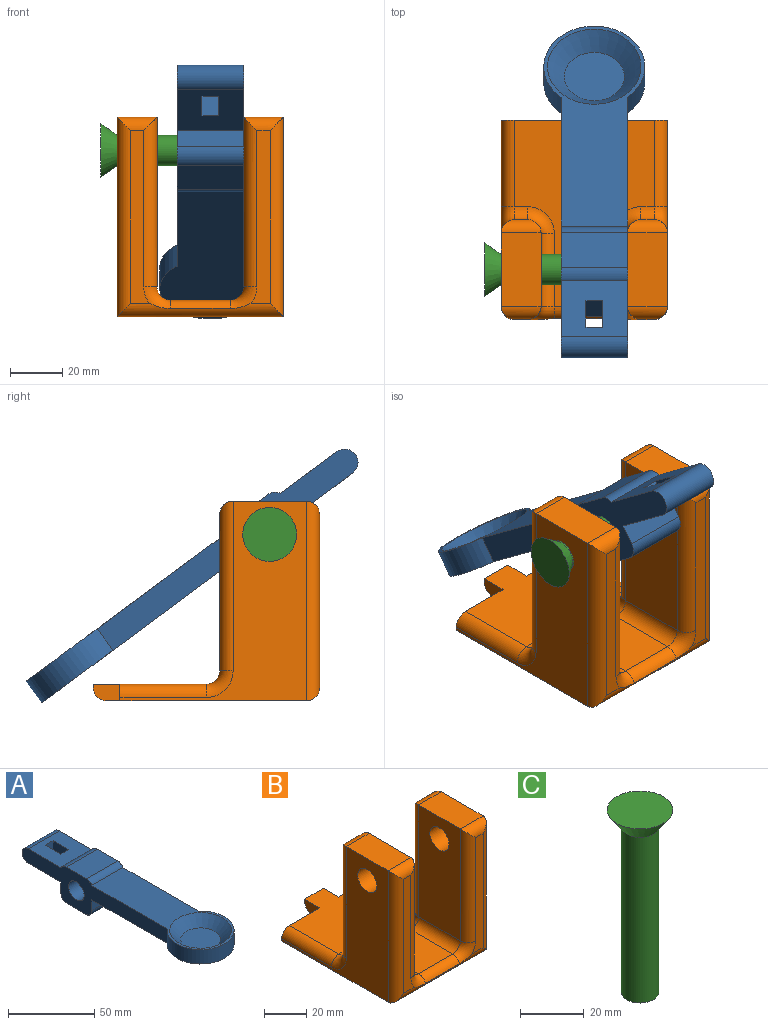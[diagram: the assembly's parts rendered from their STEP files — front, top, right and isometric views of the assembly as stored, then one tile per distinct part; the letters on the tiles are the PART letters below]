
ASSEMBLY  parts=3 mates=3
PART A: 23 faces, bbox 38.6x152.7x25.4 mm
  f0: plane 26.67x25.4mm, normal (0,0,1), area 596.8mm2, adj f2,f3,f4,f5,f7,f8,f20,f22
  f1: plane 26.67x25.4mm, normal (0,0,-1), area 596.8mm2, adj f2,f3,f4,f5,f7,f8,f12,f22
  f2: plane 12.7x10.16mm, normal (-1,0,0), area 129mm2, adj f0,f1,f3,f8
  f3: plane 10.16x6.35mm, normal (0,1,0), area 64.5mm2, adj f0,f1,f2,f4
  f4: plane 12.7x10.16mm, normal (1,0,0), area 129mm2, adj f0,f1,f3,f8
  f5: plane 118.81x25.4mm, normal (-1,0,0), area 1438.9mm2, adj f0,f1,f6,f9,f10,f11,f12,f13
  f6: cylinder r=19.3mm len=38.61mm, axis (0,0,-1), area 950.7mm2, adj f5,f7,f9,f10
  f7: plane 118.81x25.4mm, normal (1,0,0), area 1438.9mm2, adj f0,f1,f6,f9,f10,f11,f12,f13
  f8: plane 10.16x6.35mm, normal (0,-1,0), area 64.5mm2, adj f0,f1,f2,f4
  f9: plane 95.51x38.61mm, normal (0,0,1), area 1654.1mm2, adj f5,f6,f7,f17,f21
  f10: plane 95.51x38.61mm, normal (0,0,-1), area 2654.1mm2, adj f5,f6,f7,f13
  f11: plane 25.4x15.24mm, normal (0,0,-1), area 387.1mm2, adj f5,f7,f18,f19
  f12: plane 25.4x7.62mm, normal (0,1,0), area 193.5mm2, adj f1,f5,f7,f18
  f13: plane 25.4x7.62mm, normal (0,-1,0), area 193.5mm2, adj f5,f7,f10,f19
  f14: plane 25.4x16.6mm, normal (0,0,1), area 421.7mm2, adj f5,f7,f20,f21
  f15: cylinder r=6.35mm len=25.4mm, axis (1,0,0), area 1013.4mm2, adj f5,f7
  f16: plane 22.98x22.98mm, normal (0,0,1), area 414.8mm2, adj f17
  f17: cone r=8.95mm half-angle=45deg, axis (0,0,1), area 827.5mm2, adj f9,f16
  f18: cylinder r=5.08mm len=25.4mm, axis (-1,0,0), area 202.7mm2, adj f5,f7,f11,f12
  f19: cylinder r=5.08mm len=25.4mm, axis (1,0,0), area 202.7mm2, adj f5,f7,f11,f13
  f20: cylinder r=5.08mm len=25.4mm, axis (-1,0,0), area 135.1mm2, adj f0,f5,f7,f14
  f21: cylinder r=5.08mm len=25.4mm, axis (-1,0,0), area 135.1mm2, adj f5,f7,f9,f14
  f22: cylinder r=5.08mm len=25.4mm, axis (1,0,0), area 405.4mm2, adj f0,f1,f5,f7
PART B: 46 faces, bbox 63.5x86.4x79.7 mm
  f0: plane 66.04x7.31mm, normal (0,-1,0), area 340mm2, adj f31,f32,f37,f38,f42
  f1: plane 25.4x6.35mm, normal (0,1,0), area 155.8mm2, adj f2,f6,f7,f18,f20
  f2: plane 81.28x53.34mm, normal (0,0,1), area 2805.6mm2, adj f1,f5,f16,f17,f18,f20,f24,f25
  f3: plane 66.04x7.31mm, normal (0,-1,0), area 340mm2, adj f26,f27,f33,f34,f38
  f4: plane 76.2x71.12mm, normal (1,0,0), area 2079.3mm2, adj f5,f7,f13,f14,f29,f30,f32,f35
  f5: plane 25.4x6.35mm, normal (0,1,0), area 155.8mm2, adj f2,f4,f7,f16,f29
  f6: plane 76.2x71.12mm, normal (-1,0,0), area 2079.3mm2, adj f1,f7,f10,f15,f19,f20,f22,f33
  f7: plane 76.2x63.5mm, normal (0,0,-1), area 4580.6mm2, adj f1,f4,f5,f6,f16,f18,f38,f45
  f8: plane 59.69x5.08mm, normal (0,1,0), area 303.2mm2, adj f19,f21,f23,f24
  f9: plane 64.77x27.94mm, normal (1,0,0), area 1683mm2, adj f10,f15,f23,f27,f28
  f10: plane 27.94x15.24mm, normal (0,0,1), area 425.8mm2, adj f6,f9,f21,f26
  f11: plane 59.69x5.08mm, normal (0,1,0), area 303.2mm2, adj f30,f36,f40,f41
  f12: plane 64.77x27.94mm, normal (-1,0,0), area 1683mm2, adj f13,f14,f37,f41,f44
  f13: plane 27.94x15.24mm, normal (0,0,1), area 425.8mm2, adj f4,f12,f31,f36
  f14: cylinder r=6.35mm len=15.24mm, axis (1,0,0), area 608mm2, adj f4,f12
  f15: cylinder r=6.35mm len=15.24mm, axis (1,0,0), area 608mm2, adj f6,f9
  f16: plane 10.16x6.35mm, normal (1,0,0), area 59mm2, adj f2,f5,f7,f17,f45
  f17: plane 12.7x1.27mm, normal (0,1,0), area 16.1mm2, adj f2,f16,f18,f45
  f18: plane 10.16x6.35mm, normal (-1,0,0), area 59mm2, adj f1,f2,f7,f17,f45
  f19: cylinder r=5.08mm len=64.77mm, axis (0,0,-1), area 502.1mm2, adj f6,f8,f21,f22
  f20: cylinder r=5.08mm len=33.02mm, axis (0,1,0), area 263.5mm2, adj f1,f2,f6,f22
  f21: cylinder r=5.08mm len=15.24mm, axis (1,0,0), area 92.1mm2, adj f8,f10,f19,f23
  f22: torus R=10.16mm, axis (-1,0,0), area 86.8mm2, adj f6,f19,f20,f24
  f23: cylinder r=5.08mm len=64.77mm, axis (0,0,-1), area 502.1mm2, adj f8,f9,f21,f25
  f24: cylinder r=5.08mm len=5.08mm, axis (1,0,0), area 40.5mm2, adj f2,f8,f22,f25
  f25: torus R=10.16mm, axis (0,0,1), area 86.8mm2, adj f2,f23,f24,f28
  f26: cylinder r=5.08mm len=15.24mm, axis (-1,0,0), area 92.1mm2, adj f3,f10,f27,f33
  f27: cylinder r=5.08mm len=64.77mm, axis (0,0,-1), area 502.1mm2, adj f3,f9,f26,f34
  f28: cylinder r=5.08mm len=27.94mm, axis (0,-1,0), area 223mm2, adj f2,f9,f25,f34
  f29: cylinder r=5.08mm len=33.02mm, axis (0,-1,0), area 263.5mm2, adj f2,f4,f5,f35
  f30: cylinder r=5.08mm len=64.77mm, axis (0,0,-1), area 502.1mm2, adj f4,f11,f35,f36
  f31: cylinder r=5.08mm len=15.24mm, axis (-1,0,0), area 92.1mm2, adj f0,f13,f32,f37
  f32: cylinder r=5.08mm len=76.2mm, axis (0,0,1), area 578.6mm2, adj f0,f4,f31,f38
  f33: cylinder r=5.08mm len=76.2mm, axis (0,0,-1), area 578.6mm2, adj f3,f6,f26,f38
  f34: torus R=10.16mm, axis (0,-1,0), area 75.7mm2, adj f3,f27,f28,f38,f39
  f35: torus R=10.16mm, axis (-1,0,0), area 86.8mm2, adj f4,f29,f30,f40
  f36: cylinder r=5.08mm len=15.24mm, axis (1,0,0), area 92.1mm2, adj f11,f13,f30,f41
  f37: cylinder r=5.08mm len=64.77mm, axis (0,0,1), area 502.1mm2, adj f0,f12,f31,f42
  f38: cylinder r=5.08mm len=63.5mm, axis (1,0,0), area 412.1mm2, adj f0,f3,f7,f32,f33,f34,f39,f42
  f39: cylinder r=5.08mm len=22.86mm, axis (-1,0,0), area 137.8mm2, adj f2,f34,f38,f42
  f40: cylinder r=5.08mm len=5.08mm, axis (1,0,0), area 40.5mm2, adj f2,f11,f35,f43
  f41: cylinder r=5.08mm len=64.77mm, axis (0,0,-1), area 502.1mm2, adj f11,f12,f36,f43
  f42: torus R=10.16mm, axis (0,-1,0), area 75.7mm2, adj f0,f37,f38,f39,f44
  f43: torus R=10.16mm, axis (0,0,1), area 86.8mm2, adj f2,f40,f41,f44
  f44: cylinder r=5.08mm len=27.94mm, axis (0,1,0), area 223mm2, adj f2,f12,f42,f43
  f45: cylinder r=5.08mm len=12.7mm, axis (1,0,0), area 101.3mm2, adj f7,f16,f17,f18
PART C: 4 faces, bbox 20.6x20.6x69.9 mm
  f0: cylinder r=5.84mm len=63.5mm, axis (0,0,-1), area 2330.9mm2, adj f1,f2
  f1: plane 11.68x11.68mm, normal (0,0,-1), area 107.2mm2, adj f0
  f2: cone r=5.84mm half-angle=35deg, axis (0,0,1), area 392.8mm2, adj f0,f3
  f3: plane 20.58x20.58mm, normal (0,0,1), area 332.5mm2, adj f2
PLACE A rot(axis=(0,-0.31,-0.95),180deg) t=(-4.78,-19.27,64.39)mm
PLACE B t=(-8.59,-0.22,0.89)mm fixed
PLACE C rot(axis=(0,-1,0),90deg) t=(23.16,-19.27,64.39)mm
MATE fastened C.f0 <-> B.f14  axis (1,0,0) through (23.16,-19.27,64.39)mm
MATE parallel A.f15 <-> B.f14  axis (1,0,0) through (7.92,-19.27,64.39)mm
MATE cylindrical A.f15 <-> C.f0  axis (-1,0,0) through (-17.48,-19.27,64.39)mm
